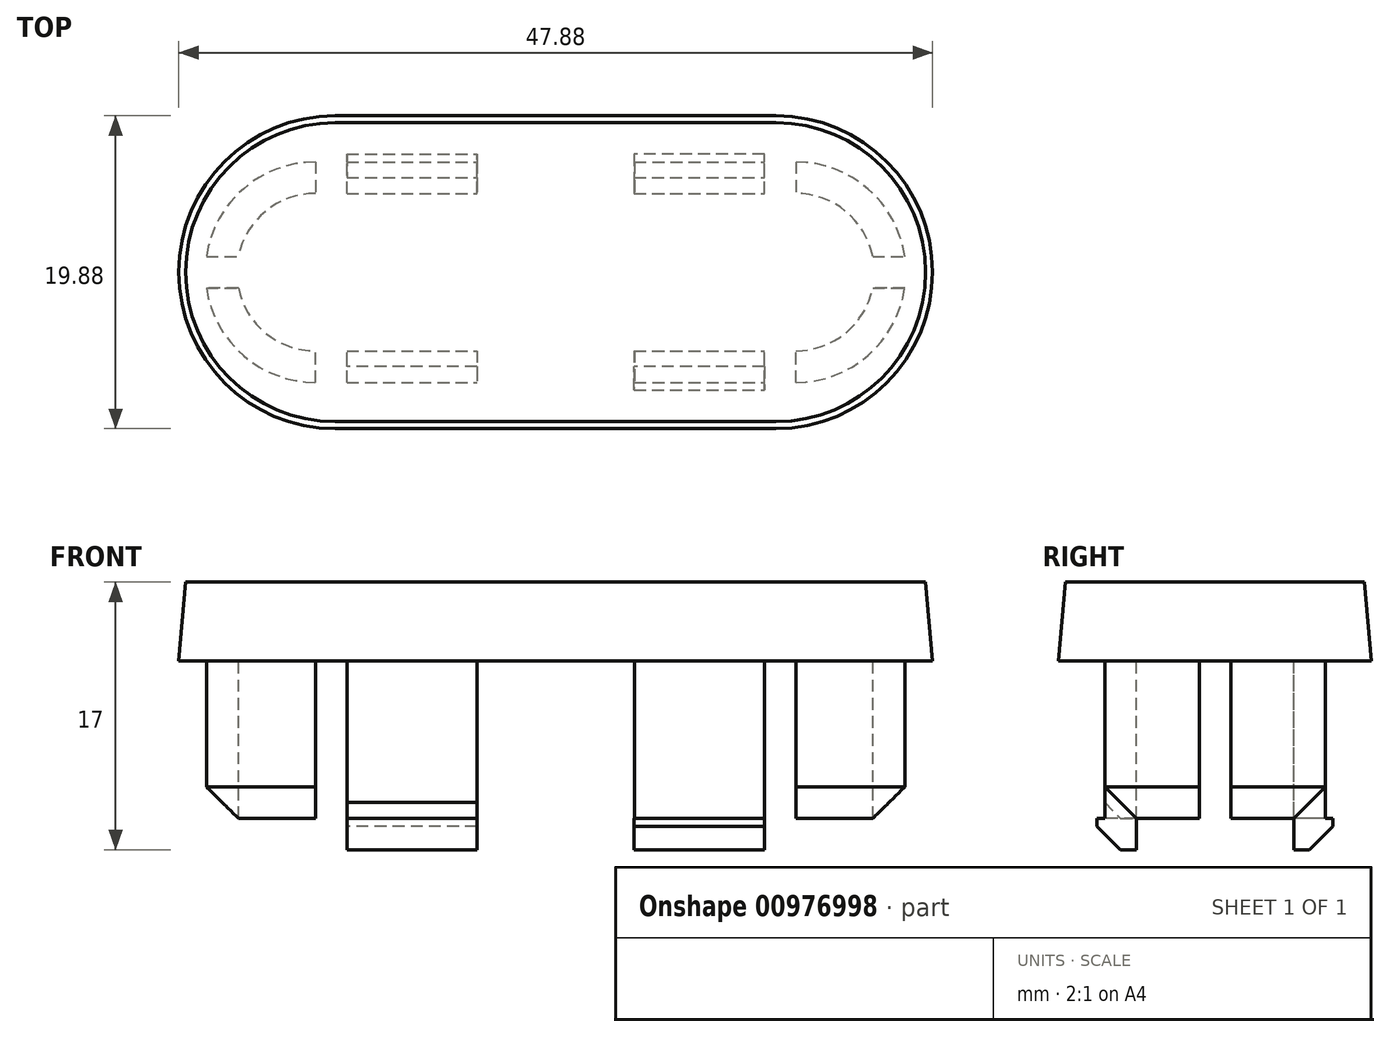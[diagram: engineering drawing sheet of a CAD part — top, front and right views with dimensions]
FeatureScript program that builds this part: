
annotation { "Feature Type Name" : "Feature", "Feature Type Description" : "" }
export const myFeature = defineFeature(function(context is Context, id is Id, definition is map)
    precondition{}
    {
        {
            var Q0;
            Q0=qCreatedBy(makeId("Top.planeOp"),FACE);
            var sketch = newSketch(context, id + "F0", { "sketchPlane" : qUnion([Q0])});
            skLineSegment(sketch, "E0.bottom", {"start": v(-14, 10) * mm, "end": v(14, 10) * mm});
            skLineSegment(sketch, "E0.top", {"start": v(-14, -10) * mm, "end": v(14, -10) * mm});
            skLineSegment(sketch, "E0.left", {"start": v(-14, 10) * mm, "end": v(-14, -10) * mm});
            skLineSegment(sketch, "E0.right", {"start": v(14, 10) * mm, "end": v(14, -10) * mm});
            skArc(sketch, "E1", {"start": v(-14, 10) * mm, "mid": v(-24, 0) * mm, "end": v(-14, -10) * mm});
            skPoint(sketch, "E2", {"position": v(14, 0) * mm});
            skArc(sketch, "E3", {"start": v(14, -10) * mm, "mid": v(24, 0) * mm, "end": v(14, 10) * mm});
            skLineSegment(sketch, "E4", {"start": v(-14, 0) * mm, "end": v(14, 0) * mm, "construction": true});
            skPoint(sketch, "E5", {"position": v(0, 0) * mm});
            skSolve(sketch);
        }
        {
            var Q0;
            Q0 = qSketchRegion(id + "F0", true);
            extrude(context, id + "F1", {"entities" : qUnion([Q0]), "depth" : 5 * mm, "offsetDistance" : 25 * mm});
        }
        {
            var Q0;
            Q0=makeQuery(id+"F1.opExtrude","CAP_FACE",FACE,{"disambiguationData":[OSD([sQuery(id+"F0.wireOp",EDGE,"E0.bottom"),sQuery(id+"F0.wireOp",EDGE,"E0.top"),sQuery(id+"F0.wireOp",EDGE,"E1"),sQuery(id+"F0.wireOp",EDGE,"E3")])],"isStart":true});
            var sketch = newSketch(context, id + "F2", { "sketchPlane" : qUnion([Q0])});
            skLineSegment(sketch, "E6.bottom", {"start": v(-15.25, 7) * mm, "end": v(15.25, 7) * mm});
            skLineSegment(sketch, "E6.top", {"start": v(-15.25, 5) * mm, "end": v(15.25, 5) * mm});
            skLineSegment(sketch, "E6.left", {"start": v(-15.25, 7) * mm, "end": v(-15.25, 5) * mm});
            skLineSegment(sketch, "E6.right", {"start": v(15.25, 7) * mm, "end": v(15.25, 5) * mm});
            skPoint(sketch, "E7", {"position": v(0, 5) * mm});
            skLineSegment(sketch, "E8.bottom", {"start": v(-15.25, -7) * mm, "end": v(15.25, -7) * mm});
            skLineSegment(sketch, "E8.top", {"start": v(-15.25, -5) * mm, "end": v(15.25, -5) * mm});
            skLineSegment(sketch, "E8.left", {"start": v(-15.25, -7) * mm, "end": v(-15.25, -5) * mm});
            skLineSegment(sketch, "E8.right", {"start": v(15.25, -7) * mm, "end": v(15.25, -5) * mm});
            skLineSegment(sketch, "E9", {"start": v(0, -7) * mm, "end": v(0, 7) * mm, "construction": true});
            skPoint(sketch, "E10", {"position": v(0, 0) * mm});
            skArc(sketch, "E11", {"start": v(-15.25, 7) * mm, "mid": v(-22.25, 0) * mm, "end": v(-15.25, -7) * mm});
            skArc(sketch, "E12", {"start": v(15.25, -7) * mm, "mid": v(22.25, 0) * mm, "end": v(15.25, 7) * mm});
            skArc(sketch, "E13", {"start": v(-15.25, 5) * mm, "mid": v(-20.25, 0) * mm, "end": v(-15.25, -5) * mm});
            skArc(sketch, "E14", {"start": v(15.25, -5) * mm, "mid": v(20.25, 0) * mm, "end": v(15.25, 5) * mm});
            skLineSegment(sketch, "E15.bottom", {"start": v(-22.75, 1) * mm, "end": v(22.62, 1) * mm});
            skLineSegment(sketch, "E15.top", {"start": v(-22.75, -1) * mm, "end": v(22.62, -1) * mm});
            skLineSegment(sketch, "E15.left", {"start": v(-22.75, 1) * mm, "end": v(-22.75, -1) * mm});
            skLineSegment(sketch, "E15.right", {"start": v(22.62, 1) * mm, "end": v(22.62, -1) * mm});
            skLineSegment(sketch, "E16", {"start": v(15.25, 5) * mm, "end": v(15.25, -5) * mm});
            skLineSegment(sketch, "E17", {"start": v(13.25, 7) * mm, "end": v(13.25, -7) * mm});
            skLineSegment(sketch, "E18", {"start": v(-15.25, 7) * mm, "end": v(-15.25, -7) * mm});
            skLineSegment(sketch, "E19", {"start": v(-13.25, 7) * mm, "end": v(-13.25, -7) * mm});
            skLineSegment(sketch, "E20.bottom", {"start": v(5, -7) * mm, "end": v(-5, -7) * mm});
            skLineSegment(sketch, "E20.top", {"start": v(5, 7) * mm, "end": v(-5, 7) * mm});
            skLineSegment(sketch, "E20.left", {"start": v(5, -7) * mm, "end": v(5, 7) * mm});
            skLineSegment(sketch, "E20.right", {"start": v(-5, -7) * mm, "end": v(-5, 7) * mm});
            skSolve(sketch);
        }
        {
            var Q0;
            {var subQ0=sQuery(id+"F2.wireOp",EDGE,"E17");var subQ1=sQuery(id+"F2.wireOp",EDGE,"E6.bottom");var subQ2=makeQuery(id+"F2.imprint","INTERSECT",VERTEX,{"derivedFrom":[subQ1,subQ0]});Q0=makeQuery(id+"F2.imprint","IMPRINT",FACE,{"disambiguationData":[TD([[makeQuery(id+"F2.imprint","IMPRINT",EDGE,{"disambiguationData":[TD([[subQ2,1.0]])],"derivedFrom":subQ1}),-1.0]])]});}
            var Q1;
            {var subQ0=sQuery(id+"F2.wireOp",EDGE,"E6.right");Q1=makeQuery(id+"F2.imprint","IMPRINT",FACE,{"disambiguationData":[TD([[makeQuery(id+"F2.imprint","IMPRINT",EDGE,{"derivedFrom":subQ0}),1.0]])]});}
            var Q2;
            {var subQ0=sQuery(id+"F2.wireOp",EDGE,"E17");var subQ1=sQuery(id+"F2.wireOp",EDGE,"E8.bottom");var subQ2=makeQuery(id+"F2.imprint","INTERSECT",VERTEX,{"derivedFrom":[subQ1,subQ0]});Q2=makeQuery(id+"F2.imprint","IMPRINT",FACE,{"disambiguationData":[TD([[makeQuery(id+"F2.imprint","IMPRINT",EDGE,{"disambiguationData":[TD([[subQ2,1.0]])],"derivedFrom":subQ1}),1.0]])]});}
            var Q3;
            {var subQ0=sQuery(id+"F2.wireOp",EDGE,"E8.right");Q3=makeQuery(id+"F2.imprint","IMPRINT",FACE,{"disambiguationData":[TD([[makeQuery(id+"F2.imprint","IMPRINT",EDGE,{"derivedFrom":subQ0}),-1.0]])]});}
            var Q4;
            {var subQ1=sQuery(id+"F2.wireOp",EDGE,"E11");var subQ3=sQuery(id+"F2.wireOp",EDGE,"E15.bottom");var subQ4=makeQuery(id+"F2.imprint","INTERSECT",VERTEX,{"derivedFrom":[subQ1,subQ3]});Q4=makeQuery(id+"F2.imprint","IMPRINT",FACE,{"disambiguationData":[TD([[makeQuery(id+"F2.imprint","IMPRINT",EDGE,{"disambiguationData":[TD([[subQ4,-1.0]])],"derivedFrom":subQ3}),1.0]])]});}
            var Q5;
            {var subQ1=sQuery(id+"F2.wireOp",EDGE,"E11");var subQ3=sQuery(id+"F2.wireOp",EDGE,"E15.top");var subQ4=makeQuery(id+"F2.imprint","INTERSECT",VERTEX,{"derivedFrom":[subQ1,subQ3]});Q5=makeQuery(id+"F2.imprint","IMPRINT",FACE,{"disambiguationData":[TD([[makeQuery(id+"F2.imprint","IMPRINT",EDGE,{"disambiguationData":[TD([[subQ4,-1.0]])],"derivedFrom":subQ3}),-1.0]])]});}
            var Q6;
            {var subQ0=sQuery(id+"F2.wireOp",EDGE,"E19");var subQ5=sQuery(id+"F2.wireOp",EDGE,"E8.top");var subQ7=makeQuery(id+"F2.imprint","INTERSECT",VERTEX,{"derivedFrom":[subQ5,subQ0]});Q6=makeQuery(id+"F2.imprint","IMPRINT",FACE,{"disambiguationData":[TD([[makeQuery(id+"F2.imprint","IMPRINT",EDGE,{"disambiguationData":[TD([[subQ7,-1.0]])],"derivedFrom":subQ5}),-1.0]])]});}
            var Q7;
            {var subQ0=sQuery(id+"F2.wireOp",EDGE,"E19");var subQ5=sQuery(id+"F2.wireOp",EDGE,"E6.top");var subQ6=makeQuery(id+"F2.imprint","INTERSECT",VERTEX,{"derivedFrom":[subQ5,subQ0]});Q7=makeQuery(id+"F2.imprint","IMPRINT",FACE,{"disambiguationData":[TD([[makeQuery(id+"F2.imprint","IMPRINT",EDGE,{"disambiguationData":[TD([[subQ6,-1.0]])],"derivedFrom":subQ5}),1.0]])]});}
            extrude(context, id + "F3", {"entities" : qUnion([Q0, Q1, Q2, Q3, Q4, Q5, Q6, Q7]), "operationType" : NewBodyOperationType.ADD, "depth" : 10 * mm, "offsetDistance" : 25 * mm});
        }
        {
            var Q0;
            Q0=makeQuery(id+"F3.opExtrude","CAP_FACE",FACE,{"disambiguationData":[OSD([sQuery(id+"F2.wireOp",EDGE,"E6.bottom"),sQuery(id+"F2.wireOp",EDGE,"E6.top"),sQuery(id+"F2.wireOp",EDGE,"E17"),sQuery(id+"F2.wireOp",EDGE,"E19")])],"isStart":false});
            var sketch = newSketch(context, id + "F4", { "sketchPlane" : qUnion([Q0])});
            skLineSegment(sketch, "E21.bottom", {"start": v(-13.25, 5) * mm, "end": v(13.25, 5) * mm});
            skLineSegment(sketch, "E21.top", {"start": v(-13.25, 7.5) * mm, "end": v(13.25, 7.5) * mm});
            skLineSegment(sketch, "E21.left", {"start": v(-13.25, 5) * mm, "end": v(-13.25, 7.5) * mm});
            skLineSegment(sketch, "E21.right", {"start": v(13.25, 5) * mm, "end": v(13.25, 7.5) * mm});
            skLineSegment(sketch, "E22.bottom", {"start": v(-13.25, -5) * mm, "end": v(13.25, -5) * mm});
            skLineSegment(sketch, "E22.top", {"start": v(-13.25, -7.5) * mm, "end": v(13.25, -7.5) * mm});
            skLineSegment(sketch, "E22.left", {"start": v(-13.25, -5) * mm, "end": v(-13.25, -7.5) * mm});
            skLineSegment(sketch, "E22.right", {"start": v(13.25, -5) * mm, "end": v(13.25, -7.5) * mm});
            skLineSegment(sketch, "E23", {"start": v(4.98, -7.5) * mm, "end": v(4.98, 7.5) * mm});
            skLineSegment(sketch, "E24", {"start": v(-5, -7.5) * mm, "end": v(-5.04, 7.5) * mm});
            skSolve(sketch);
        }
        {
            var Q0;
            {var subQ4=sQuery(id+"F2.wireOp",EDGE,"E6.bottom");var subQ7=makeQuery(id+"F3.opExtrude","CAP_EDGE",EDGE,{"disambiguationData":[OSD([subQ4]),TDD([makeQuery(id+"F2.imprint","IMPRINT",EDGE,{"disambiguationData":[TD([[makeQuery(id+"F2.imprint","INTERSECT",VERTEX,{"derivedFrom":[subQ4,sQuery(id+"F2.wireOp",EDGE,"E19")]}),-1.0]])],"derivedFrom":subQ4})])],"isStart":false});Q0=makeQuery(id+"F4.imprint","IMPRINT",FACE,{"disambiguationData":[TD([[makeQuery(id+"F4.imprint","IMPRINT",EDGE,{"derivedFrom":subQ7}),-1.0]])]});}
            var Q1;
            {var subQ2=sQuery(id+"F2.wireOp",EDGE,"E6.bottom");var subQ7=makeQuery(id+"F3.opExtrude","CAP_EDGE",EDGE,{"disambiguationData":[OSD([subQ2]),TDD([makeQuery(id+"F2.imprint","IMPRINT",EDGE,{"disambiguationData":[TD([[makeQuery(id+"F2.imprint","INTERSECT",VERTEX,{"derivedFrom":[subQ2,sQuery(id+"F2.wireOp",EDGE,"E17")]}),1.0]])],"derivedFrom":subQ2})])],"isStart":false});Q1=makeQuery(id+"F4.imprint","IMPRINT",FACE,{"disambiguationData":[TD([[makeQuery(id+"F4.imprint","IMPRINT",EDGE,{"derivedFrom":subQ7}),-1.0]])]});}
            var Q2;
            {var subQ0=sQuery(id+"F4.wireOp",EDGE,"E22.left");Q2=makeQuery(id+"F4.imprint","IMPRINT",FACE,{"disambiguationData":[TD([[makeQuery(id+"F4.imprint","IMPRINT",EDGE,{"derivedFrom":subQ0}),1.0]])]});}
            var Q3;
            {var subQ0=sQuery(id+"F4.wireOp",EDGE,"E22.right");Q3=makeQuery(id+"F4.imprint","IMPRINT",FACE,{"disambiguationData":[TD([[makeQuery(id+"F4.imprint","IMPRINT",EDGE,{"derivedFrom":subQ0}),-1.0]])]});}
            var Q4;
            {var subQ1=sQuery(id+"F2.wireOp",EDGE,"E6.bottom");var subQ4=makeQuery(id+"F3.opExtrude","CAP_EDGE",EDGE,{"disambiguationData":[OSD([subQ1]),TDD([makeQuery(id+"F2.imprint","IMPRINT",EDGE,{"disambiguationData":[TD([[makeQuery(id+"F2.imprint","INTERSECT",VERTEX,{"derivedFrom":[subQ1,sQuery(id+"F2.wireOp",EDGE,"E19")]}),-1.0]])],"derivedFrom":subQ1})])],"isStart":false});Q4=makeQuery(id+"F4.imprint","IMPRINT",FACE,{"disambiguationData":[TD([[makeQuery(id+"F4.imprint","IMPRINT",EDGE,{"derivedFrom":subQ4}),1.0]])]});}
            var Q5;
            {var subQ1=sQuery(id+"F2.wireOp",EDGE,"E6.bottom");var subQ4=makeQuery(id+"F3.opExtrude","CAP_EDGE",EDGE,{"disambiguationData":[OSD([subQ1]),TDD([makeQuery(id+"F2.imprint","IMPRINT",EDGE,{"disambiguationData":[TD([[makeQuery(id+"F2.imprint","INTERSECT",VERTEX,{"derivedFrom":[subQ1,sQuery(id+"F2.wireOp",EDGE,"E17")]}),1.0]])],"derivedFrom":subQ1})])],"isStart":false});Q5=makeQuery(id+"F4.imprint","IMPRINT",FACE,{"disambiguationData":[TD([[makeQuery(id+"F4.imprint","IMPRINT",EDGE,{"derivedFrom":subQ4}),1.0]])]});}
            extrude(context, id + "F5", {"entities" : qUnion([Q0, Q1, Q2, Q3, Q4, Q5]), "operationType" : NewBodyOperationType.ADD, "depth" : 2 * mm, "offsetDistance" : 25 * mm});
        }
        {
            var Q0;
            Q0=makeQuery(id+"F5.opExtrude","CAP_EDGE",EDGE,{"disambiguationData":[OSD([sQuery(id+"F4.wireOp",EDGE,"E22.top")])],"isStart":false});
            var Q1;
            Q1=makeQuery(id+"F5.opExtrude","CAP_EDGE",EDGE,{"disambiguationData":[OSD([sQuery(id+"F4.wireOp",EDGE,"E21.top")])],"isStart":false});
            chamfer(context, id + "F6", {"entities" : qUnion([Q0, Q1]), "width" : 1.5 * mm, "tangentPropagation" : true});
        }
        {
            var Q0;
            Q0=makeQuery(id+"F1.opExtrude","CAP_EDGE",EDGE,{"disambiguationData":[OSD([sQuery(id+"F0.wireOp",EDGE,"E1")])],"isStart":false});
            chamfer(context, id + "F7", {"entities" : qUnion([Q0]), "chamferType" : ChamferType.OFFSET_ANGLE, "width" : 0.5 * mm, "oppositeDirection" : false, "angle" : 85 * degree, "tangentPropagation" : true});
        }
        {
            var Q0;
            Q0=makeQuery(id+"F3.opExtrude","CAP_EDGE",EDGE,{"disambiguationData":[OSD([sQuery(id+"F2.wireOp",EDGE,"E8.bottom")])],"isStart":false});
            var Q1;
            {var subQ0=sQuery(id+"F2.wireOp",EDGE,"E6.bottom");Q1=makeQuery(id+"F3.opExtrude","CAP_EDGE",EDGE,{"disambiguationData":[OSD([subQ0]),TDD([makeQuery(id+"F2.imprint","IMPRINT",EDGE,{"disambiguationData":[TD([[makeQuery(id+"F2.imprint","INTERSECT",VERTEX,{"derivedFrom":[subQ0,sQuery(id+"F2.wireOp",EDGE,"E17")]}),1.0]])],"derivedFrom":subQ0})])],"isStart":false});}
            var Q2;
            {var subQ0=sQuery(id+"F2.wireOp",EDGE,"E6.bottom");Q2=makeQuery(id+"F3.opExtrude","CAP_EDGE",EDGE,{"disambiguationData":[OSD([subQ0]),TDD([makeQuery(id+"F2.imprint","IMPRINT",EDGE,{"disambiguationData":[TD([[makeQuery(id+"F2.imprint","INTERSECT",VERTEX,{"derivedFrom":[subQ0,sQuery(id+"F2.wireOp",EDGE,"E19")]}),-1.0]])],"derivedFrom":subQ0})])],"isStart":false});}
            chamfer(context, id + "F8", {"entities" : qUnion([Q0, Q1, Q2]), "width" : 1 * mm, "tangentPropagation" : true});
        }
        {
            var Q0;
            {var subQ0=sQuery(id+"F2.wireOp",EDGE,"E12");Q0=makeQuery(id+"F3.opExtrude","CAP_EDGE",EDGE,{"disambiguationData":[OSD([subQ0]),TDD([makeQuery(id+"F2.imprint","IMPRINT",EDGE,{"disambiguationData":[TD([[makeQuery(id+"F2.imprint","INTERSECT",VERTEX,{"derivedFrom":[subQ0,sQuery(id+"F2.wireOp",EDGE,"E15.bottom")]}),-1.0]])],"derivedFrom":subQ0})])],"isStart":false});}
            var Q1;
            {var subQ0=sQuery(id+"F2.wireOp",EDGE,"E12");Q1=makeQuery(id+"F3.opExtrude","CAP_EDGE",EDGE,{"disambiguationData":[OSD([subQ0]),TDD([makeQuery(id+"F2.imprint","IMPRINT",EDGE,{"disambiguationData":[TD([[makeQuery(id+"F2.imprint","INTERSECT",VERTEX,{"derivedFrom":[subQ0,sQuery(id+"F2.wireOp",EDGE,"E15.top")]}),1.0]])],"derivedFrom":subQ0})])],"isStart":false});}
            var Q2;
            {var subQ0=sQuery(id+"F2.wireOp",EDGE,"E11");Q2=makeQuery(id+"F3.opExtrude","CAP_EDGE",EDGE,{"disambiguationData":[OSD([subQ0]),TDD([makeQuery(id+"F2.imprint","IMPRINT",EDGE,{"disambiguationData":[TD([[makeQuery(id+"F2.imprint","INTERSECT",VERTEX,{"derivedFrom":[subQ0,sQuery(id+"F2.wireOp",EDGE,"E15.top")]}),-1.0]])],"derivedFrom":subQ0})])],"isStart":false});}
            var Q3;
            {var subQ0=sQuery(id+"F2.wireOp",EDGE,"E11");Q3=makeQuery(id+"F3.opExtrude","CAP_EDGE",EDGE,{"disambiguationData":[OSD([subQ0]),TDD([makeQuery(id+"F2.imprint","IMPRINT",EDGE,{"disambiguationData":[TD([[makeQuery(id+"F2.imprint","INTERSECT",VERTEX,{"derivedFrom":[subQ0,sQuery(id+"F2.wireOp",EDGE,"E15.bottom")]}),1.0]])],"derivedFrom":subQ0})])],"isStart":false});}
            chamfer(context, id + "F9", {"entities" : qUnion([Q0, Q1, Q2, Q3]), "width" : 2 * mm, "tangentPropagation" : true});
        }
    });
